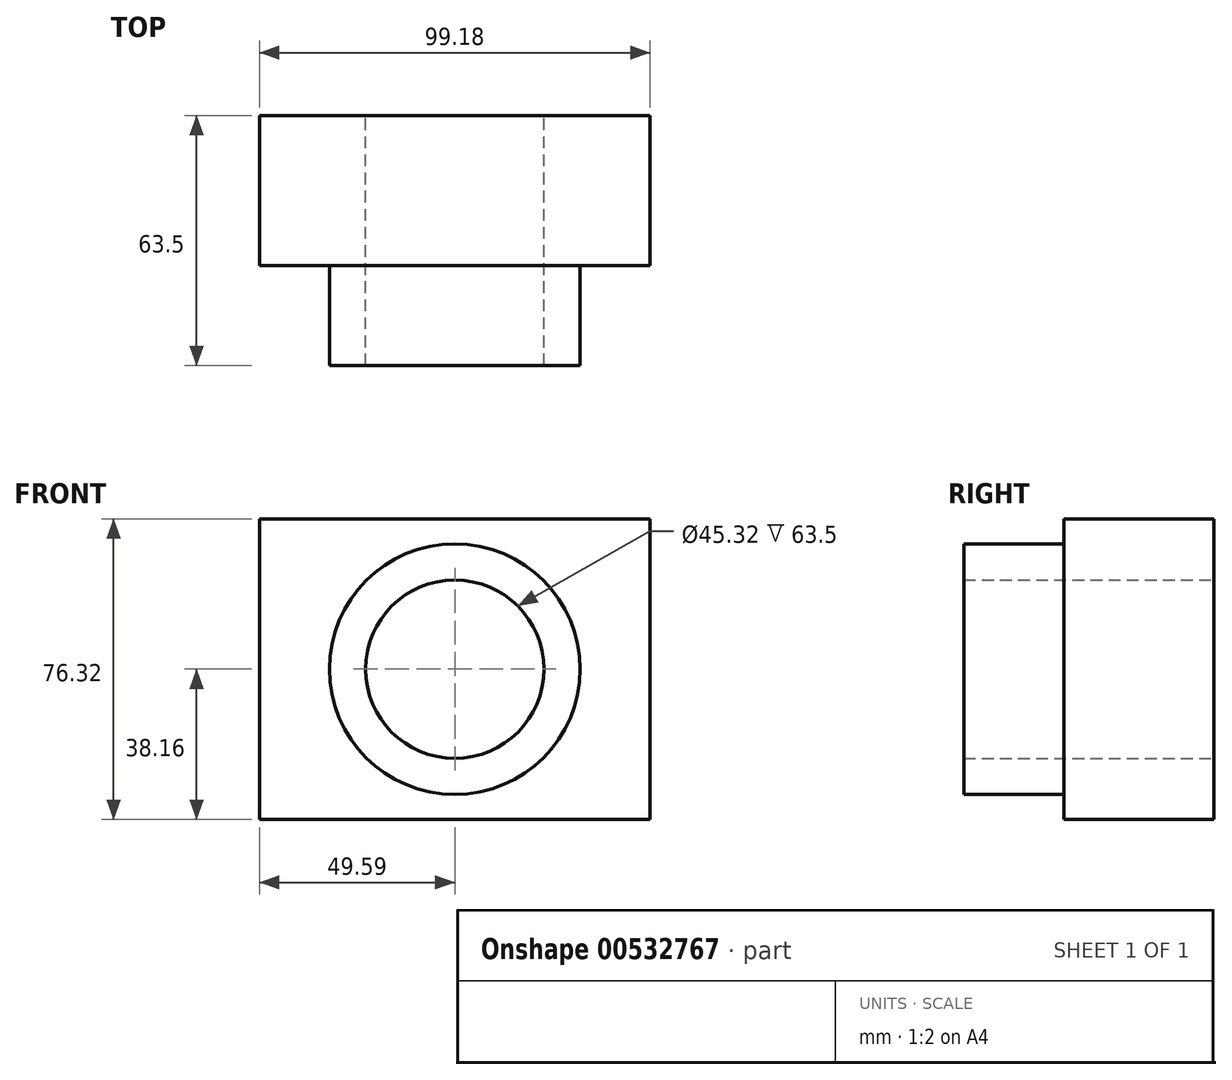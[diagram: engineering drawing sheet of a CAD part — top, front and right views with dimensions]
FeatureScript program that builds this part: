
annotation { "Feature Type Name" : "Feature", "Feature Type Description" : "" }
export const myFeature = defineFeature(function(context is Context, id is Id, definition is map)
    precondition{}
    {
        {
            var Q0;
            Q0=qCreatedBy(makeId("Front.planeOp"),FACE);
            var sketch = newSketch(context, id + "F0", { "sketchPlane" : qUnion([Q0])});
            skLineSegment(sketch, "E0.bottom", {"start": v(-49.6, 38.16) * mm, "end": v(49.6, 38.16) * mm});
            skLineSegment(sketch, "E0.top", {"start": v(-49.6, -38.16) * mm, "end": v(49.6, -38.16) * mm});
            skLineSegment(sketch, "E0.left", {"start": v(-49.6, 38.16) * mm, "end": v(-49.6, -38.16) * mm});
            skLineSegment(sketch, "E0.right", {"start": v(49.6, 38.16) * mm, "end": v(49.6, -38.16) * mm});
            skPoint(sketch, "E0.middle", {"position": v(0, 0) * mm});
            skSolve(sketch);
        }
        {
            var Q0;
            Q0=makeQuery(id+"F0.imprint","IMPRINT",FACE,{"disambiguationData":[TD([[makeQuery(id+"F0.imprint","IMPRINT",EDGE,{"derivedFrom":sQuery(id+"F0.wireOp",EDGE,"E0.bottom")}),-1.0]])]});
            extrude(context, id + "F1", {"entities" : qUnion([Q0]), "depth" : 38.1 * mm, "offsetDistance" : 25.4 * mm});
        }
        {
            var Q0;
            Q0=makeQuery(id+"F1.opExtrude","CAP_FACE",FACE,{"disambiguationData":[OSD([sQuery(id+"F0.wireOp",EDGE,"E0.bottom"),sQuery(id+"F0.wireOp",EDGE,"E0.top"),sQuery(id+"F0.wireOp",EDGE,"E0.left"),sQuery(id+"F0.wireOp",EDGE,"E0.right")])],"isStart":false});
            var sketch = newSketch(context, id + "F2", { "sketchPlane" : qUnion([Q0])});
            skCircle(sketch, "E1", {"center": v(0, 0) * mm, "radius": 31.84 * mm});
            skCircle(sketch, "E2", {"center": v(0, 0) * mm, "radius": 22.66 * mm});
            skSolve(sketch);
        }
        {
            var Q0;
            Q0 = qSketchRegion(id + "F2", true);
            extrude(context, id + "F3", {"entities" : qUnion([Q0]), "operationType" : NewBodyOperationType.ADD, "depth" : 25.4 * mm, "offsetDistance" : 25.4 * mm});
        }
        {
            var Q0;
            Q0=makeQuery(id+"F3.boolean.opBoolean","SPLIT",FACE,{"disambiguationData":[TD([makeQuery(id+"F3.opExtrude","SWEPT_FACE",FACE,{"disambiguationData":[OSD([sQuery(id+"F2.wireOp",EDGE,"E2")])]})])],"derivedFrom":makeQuery(id+"F1.opExtrude","CAP_FACE",FACE,{"disambiguationData":[OSD([sQuery(id+"F0.wireOp",EDGE,"E0.bottom"),sQuery(id+"F0.wireOp",EDGE,"E0.top"),sQuery(id+"F0.wireOp",EDGE,"E0.left"),sQuery(id+"F0.wireOp",EDGE,"E0.right")])],"isStart":false})});
            var sketch = newSketch(context, id + "F4", { "sketchPlane" : qUnion([Q0])});
            skSolve(sketch);
        }
        {
            var Q0;
            Q0=makeQuery(id+"F4.imprint","IMPRINT",FACE,{"disambiguationData":[TD([[makeQuery(id+"F4.imprint","IMPRINT",EDGE,{"derivedFrom":makeQuery(id+"F3.opExtrude","CAP_EDGE",EDGE,{"disambiguationData":[OSD([sQuery(id+"F2.wireOp",EDGE,"E2")])],"isStart":true})}),1.0]])]});
            extrude(context, id + "F5", {"entities" : qUnion([Q0]), "operationType" : NewBodyOperationType.REMOVE, "oppositeDirection" : true, "depth" : 76.2 * mm, "offsetDistance" : 25.4 * mm});
        }
    });
